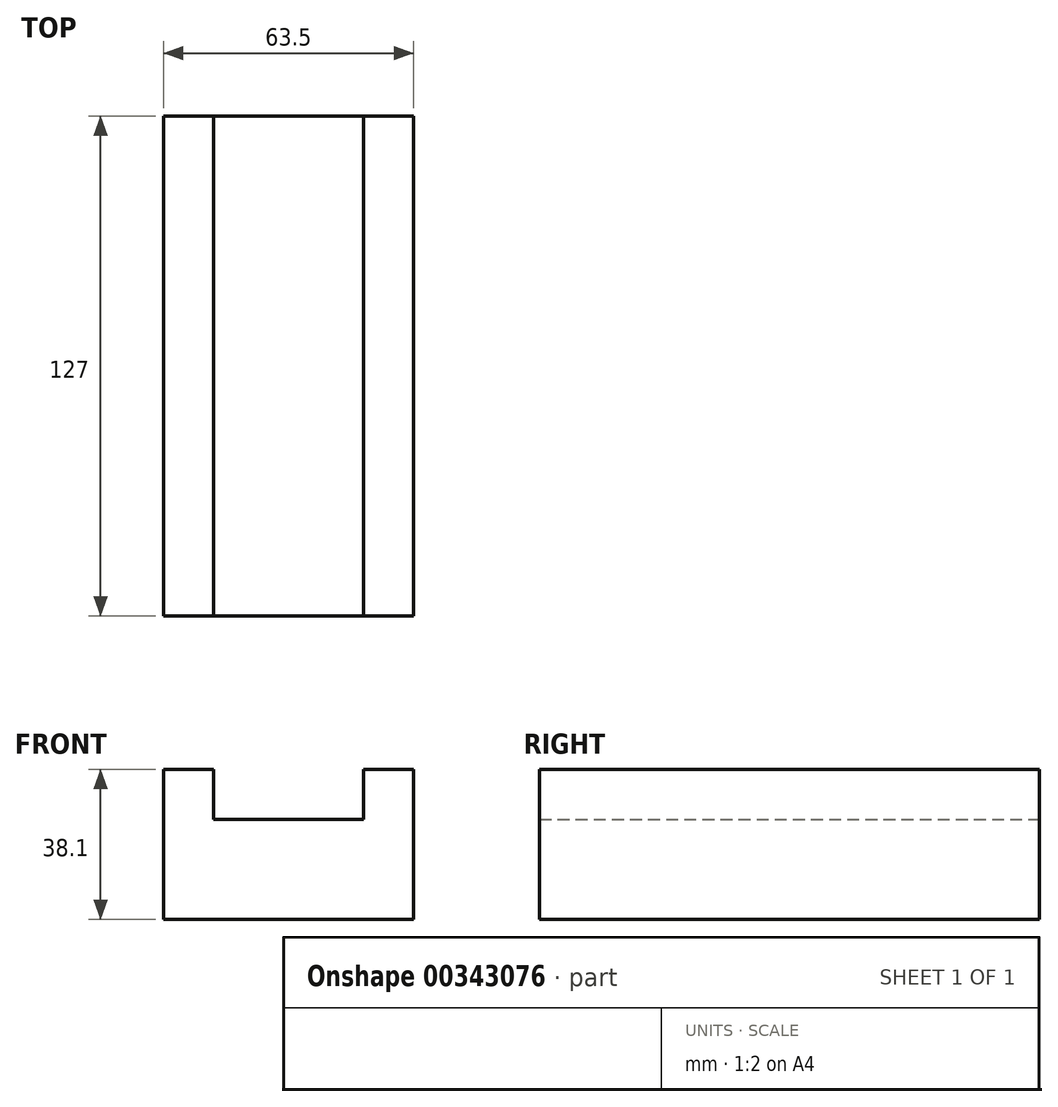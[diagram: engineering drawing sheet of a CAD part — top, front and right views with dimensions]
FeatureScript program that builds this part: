
annotation { "Feature Type Name" : "Feature", "Feature Type Description" : "" }
export const myFeature = defineFeature(function(context is Context, id is Id, definition is map)
    precondition{}
    {
        {
            var Q0;
            Q0=qCreatedBy(makeId("Front.planeOp"),FACE);
            var sketch = newSketch(context, id + "F0", { "sketchPlane" : qUnion([Q0])});
            skLineSegment(sketch, "E0", {"start": v(-32.07, -50.28) * mm, "end": v(31.43, -50.28) * mm});
            skLineSegment(sketch, "E1", {"start": v(31.43, -50.28) * mm, "end": v(31.43, -12.18) * mm});
            skLineSegment(sketch, "E2", {"start": v(31.43, -12.18) * mm, "end": v(18.73, -12.18) * mm});
            skPoint(sketch, "E3.endSnap0", {"position": v(-0.32, -50.28) * mm});
            skLineSegment(sketch, "E4", {"start": v(18.73, -12.18) * mm, "end": v(18.73, -24.88) * mm});
            skLineSegment(sketch, "E5", {"start": v(-32.07, -50.28) * mm, "end": v(-32.07, -12.18) * mm});
            skLineSegment(sketch, "E6", {"start": v(-32.07, -12.18) * mm, "end": v(-19.37, -12.18) * mm});
            skLineSegment(sketch, "E7", {"start": v(-19.37, -12.18) * mm, "end": v(-19.37, -24.88) * mm});
            skLineSegment(sketch, "E8", {"start": v(-19.37, -24.88) * mm, "end": v(18.73, -24.88) * mm});
            skPoint(sketch, "E3.end.orphan", {"position": v(-0.32, -24.88) * mm});
            skPoint(sketch, "E3.start.orphan", {"position": v(0, -50.28) * mm});
            skSolve(sketch);
        }
        {
            var Q0;
            Q0 = qSketchRegion(id + "F0", true);
            extrude(context, id + "F1", {"entities" : qUnion([Q0]), "depth" : 127 * mm});
        }
    });
